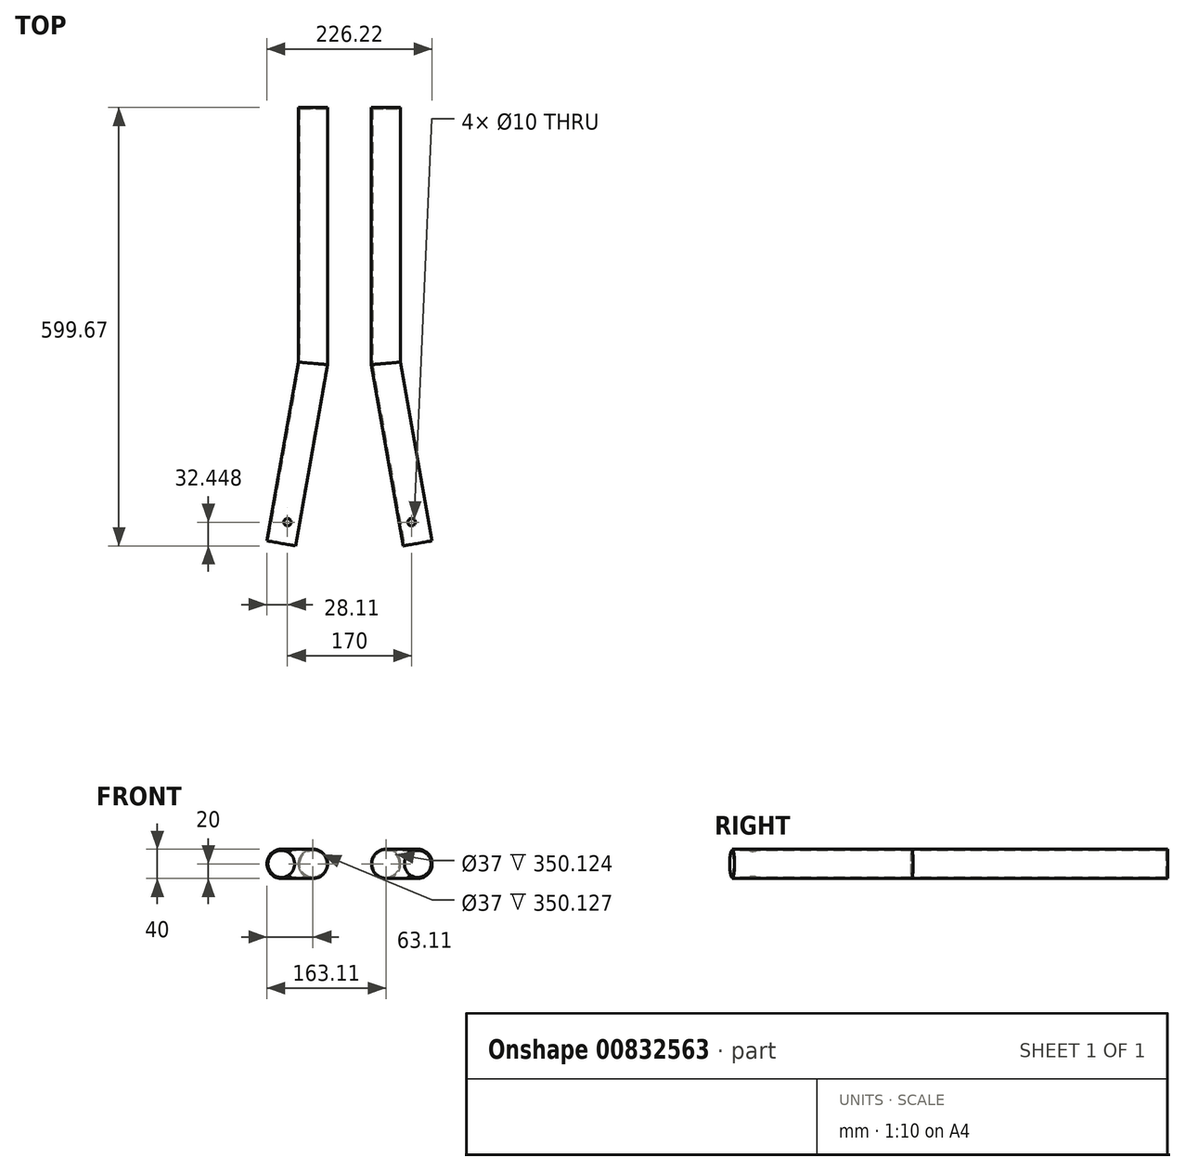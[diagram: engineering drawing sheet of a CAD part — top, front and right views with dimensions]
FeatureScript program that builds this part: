
annotation { "Feature Type Name" : "Feature", "Feature Type Description" : "" }
export const myFeature = defineFeature(function(context is Context, id is Id, definition is map)
    precondition{}
    {
        {
            var Q0;
            Q0=qCreatedBy(makeId("Front.planeOp"),FACE);
            var sketch = newSketch(context, id + "F0", { "sketchPlane" : qUnion([Q0])});
            skCircle(sketch, "E0", {"center": v(50, 0) * mm, "radius": 20 * mm});
            skSolve(sketch);
        }
        {
            var Q0;
            Q0=qCreatedBy(makeId("Top.planeOp"),FACE);
            var sketch = newSketch(context, id + "F1", { "sketchPlane" : qUnion([Q0])});
            skLineSegment(sketch, "E1", {"start": v(50, 0) * mm, "end": v(50, -350) * mm});
            skLineSegment(sketch, "E2", {"start": v(50, -350) * mm, "end": v(93.41, -596.2) * mm});
            skSolve(sketch);
        }
        {
            var Q0;
            Q0=makeQuery(id+"F0.imprint","IMPRINT",FACE,{"disambiguationData":[TD([[makeQuery(id+"F0.imprint","IMPRINT",EDGE,{"derivedFrom":sQuery(id+"F0.wireOp",EDGE,"E0")}),1.0]])]});
            var Q1;
            Q1=sQuery(id+"F1.wireOp",EDGE,"E1");
            var Q2;
            Q2=sQuery(id+"F1.wireOp",EDGE,"E2");
            sweep(context, id + "F2", {"profiles" : qUnion([Q0]), "path" : qUnion([Q1, Q2])});
        }
        {
            var Q0;
            Q0=qCreatedBy(makeId("Top.planeOp"),FACE);
            cPlane(context, id + "F3", {"entities" : qUnion([Q0]), "cplaneType" : CPlaneType.OFFSET, "offset" : 20 * mm, "width" : 150 * mm, "height" : 150 * mm});
        }
        {
            var Q0;
            Q0=qCreatedBy(id+"F3.planeOp",FACE);
            var sketch = newSketch(context, id + "F4", { "sketchPlane" : qUnion([Q0])});
            skCircle(sketch, "E3", {"center": v(85, -567.22) * mm, "radius": 5 * mm});
            skSolve(sketch);
        }
        {
            var Q0;
            Q0=makeQuery(id+"F2.opSweep","CAP_FACE",FACE,{"disambiguationData":[OSD([sQuery(id+"F0.wireOp",EDGE,"E0"),sQuery(id+"F1.wireOp",VERTEX,"E2.end")])],"isStart":false});
            shell(context, id + "F5", {"entities" : qUnion([Q0]), "thickness" : 1.5 * mm});
        }
        {
            var Q0;
            Q0=makeQuery(id+"F4.imprint","IMPRINT",FACE,{"disambiguationData":[TD([[makeQuery(id+"F4.imprint","IMPRINT",EDGE,{"derivedFrom":sQuery(id+"F4.wireOp",EDGE,"E3")}),1.0]])]});
            extrude(context, id + "F6", {"entities" : qUnion([Q0]), "operationType" : NewBodyOperationType.REMOVE, "oppositeDirection" : true, "depth" : 50 * mm, "offsetDistance" : 25 * mm});
        }
        {
            var Q0;
            Q0=makeQuery(id+"F2.opSweep","SWEPT_BODY",BODY,{"disambiguationData":[OSD([sQuery(id+"F0.wireOp",EDGE,"E0"),sQuery(id+"F1.wireOp",EDGE,"E2")])]});
            var Q1;
            Q1=qCreatedBy(makeId("Right.planeOp"),FACE);
            mirror(context, id + "F7", {"entities" : qUnion([Q0]), "mirrorPlane" : qUnion([Q1])});
        }
    });
